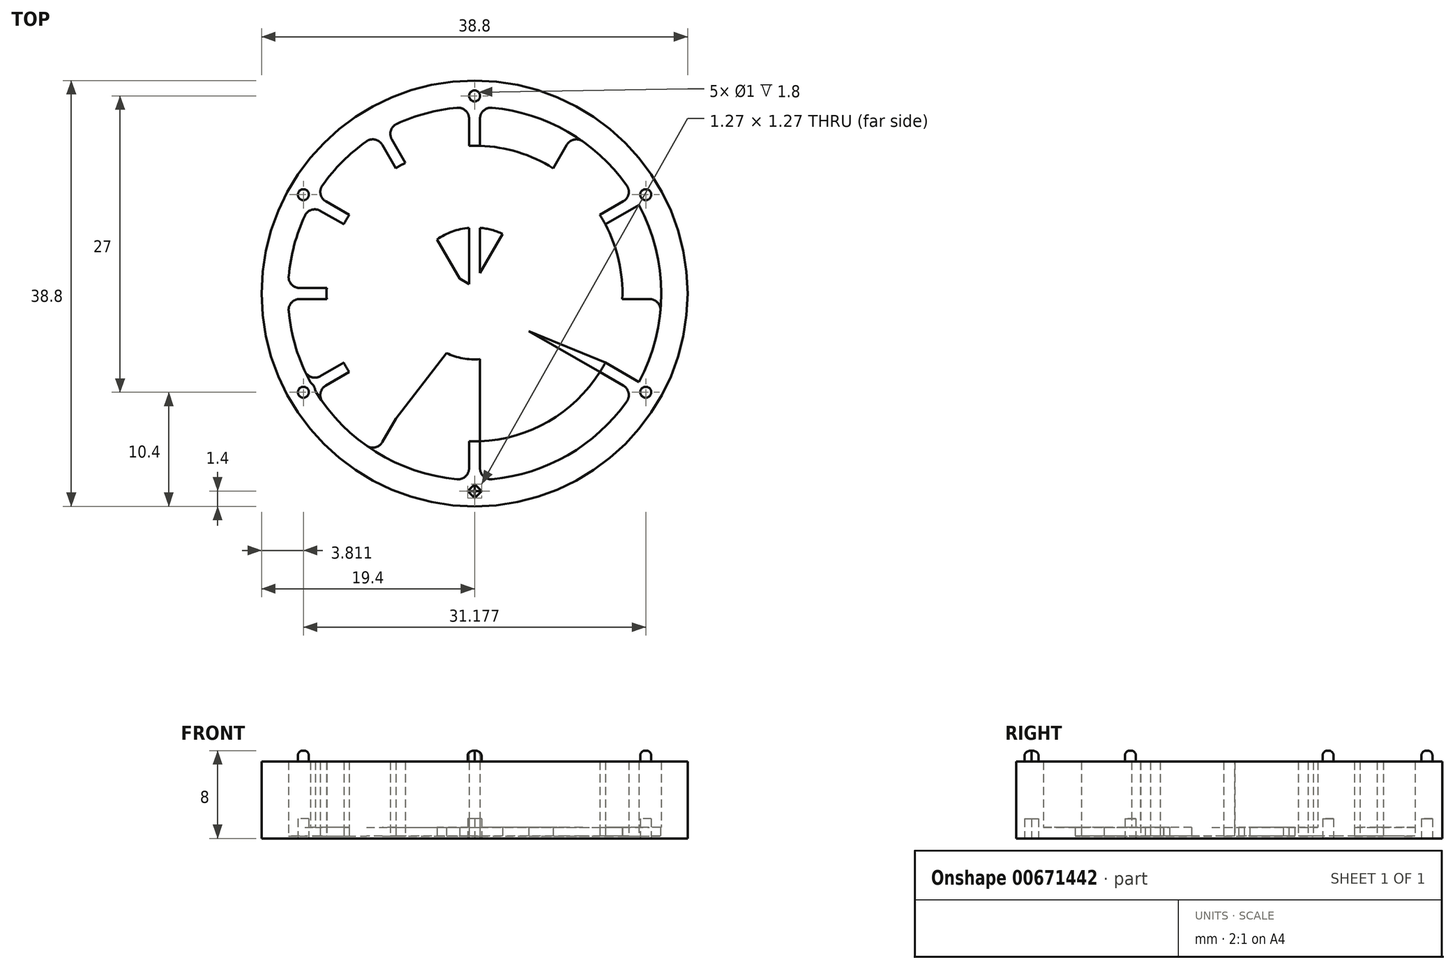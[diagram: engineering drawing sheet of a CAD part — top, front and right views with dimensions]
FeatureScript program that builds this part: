
annotation { "Feature Type Name" : "Feature", "Feature Type Description" : "" }
export const myFeature = defineFeature(function(context is Context, id is Id, definition is map)
    precondition{}
    {
        {
            var Q0;
            Q0=qCreatedBy(makeId("Top.planeOp"),FACE);
            var sketch = newSketch(context, id + "F0", { "sketchPlane" : qUnion([Q0])});
            skCircle(sketch, "E0", {"center": v(0, 0) * mm, "radius": 18 * mm});
            skCircle(sketch, "E1.0", {"center": v(0, 0) * mm, "radius": 17 * mm});
            skLineSegment(sketch, "E2.bottom", {"start": v(8.56, 15.83) * mm, "end": v(9.43, 15.33) * mm});
            skLineSegment(sketch, "E2.top", {"start": v(-9.43, -15.33) * mm, "end": v(-8.56, -15.83) * mm});
            skLineSegment(sketch, "E2.left", {"start": v(8.56, 15.83) * mm, "end": v(-9.43, -15.33) * mm});
            skLineSegment(sketch, "E2.right", {"start": v(9.43, 15.33) * mm, "end": v(-8.56, -15.83) * mm});
            skLineSegment(sketch, "E3.bottom", {"start": v(15.33, 9.43) * mm, "end": v(15.83, 8.56) * mm});
            skLineSegment(sketch, "E3.top", {"start": v(-15.83, -8.56) * mm, "end": v(-15.33, -9.43) * mm});
            skLineSegment(sketch, "E3.left", {"start": v(15.33, 9.43) * mm, "end": v(-15.83, -8.56) * mm});
            skLineSegment(sketch, "E3.right", {"start": v(15.83, 8.56) * mm, "end": v(-15.33, -9.43) * mm});
            skLineSegment(sketch, "E4", {"start": v(-38.35, 0) * mm, "end": v(39.17, 0) * mm, "construction": true});
            skLineSegment(sketch, "E5", {"start": v(0, 42.5) * mm, "end": v(0, -42.47) * mm, "construction": true});
            skLineSegment(sketch, "E6.bottom", {"start": v(-18, 0.5) * mm, "end": v(18, 0.5) * mm});
            skLineSegment(sketch, "E6.top", {"start": v(-18, -0.5) * mm, "end": v(18, -0.5) * mm});
            skLineSegment(sketch, "E6.left", {"start": v(-18, 0.5) * mm, "end": v(-18, -0.5) * mm});
            skLineSegment(sketch, "E6.right", {"start": v(18, 0.5) * mm, "end": v(18, -0.5) * mm});
            skLineSegment(sketch, "E7.bottom", {"start": v(-15.33, 9.43) * mm, "end": v(15.83, -8.56) * mm});
            skLineSegment(sketch, "E7.top", {"start": v(-15.83, 8.56) * mm, "end": v(15.33, -9.43) * mm});
            skLineSegment(sketch, "E7.left", {"start": v(-15.33, 9.43) * mm, "end": v(-15.83, 8.56) * mm});
            skLineSegment(sketch, "E7.right", {"start": v(15.83, -8.56) * mm, "end": v(15.33, -9.43) * mm});
            skLineSegment(sketch, "E8.bottom", {"start": v(-0.5, 18) * mm, "end": v(0.5, 18) * mm});
            skLineSegment(sketch, "E8.top", {"start": v(-0.5, -18) * mm, "end": v(0.5, -18) * mm});
            skLineSegment(sketch, "E8.left", {"start": v(-0.5, 18) * mm, "end": v(-0.5, -18) * mm});
            skLineSegment(sketch, "E8.right", {"start": v(0.5, 18) * mm, "end": v(0.5, -18) * mm});
            skLineSegment(sketch, "E9.bottom", {"start": v(-9.43, 15.33) * mm, "end": v(-8.56, 15.83) * mm});
            skLineSegment(sketch, "E9.top", {"start": v(8.56, -15.83) * mm, "end": v(9.43, -15.33) * mm});
            skLineSegment(sketch, "E9.left", {"start": v(-9.43, 15.33) * mm, "end": v(8.56, -15.83) * mm});
            skLineSegment(sketch, "E9.right", {"start": v(-8.56, 15.83) * mm, "end": v(9.43, -15.33) * mm});
            skCircle(sketch, "E10", {"center": v(0, 0) * mm, "radius": 13.47 * mm});
            skCircle(sketch, "E11", {"center": v(0, 0) * mm, "radius": 6 * mm});
            skLineSegment(sketch, "E12", {"start": v(-7.16, -11.4) * mm, "end": v(-2.56, -5.43) * mm});
            skLineSegment(sketch, "E13", {"start": v(4.93, -3.42) * mm, "end": v(11.9, -6.3) * mm});
            skSolve(sketch);
        }
        {
            var Q0;
            Q0=qCreatedBy(makeId("Top.planeOp"),FACE);
            var sketch = newSketch(context, id + "F1", { "sketchPlane" : qUnion([Q0])});
            skCircle(sketch, "E14", {"center": v(0, 0) * mm, "radius": 19.4 * mm});
            skCircle(sketch, "E15", {"center": v(0, 0) * mm, "radius": 17 * mm});
            skSolve(sketch);
        }
        {
            var Q0;
            Q0=makeQuery(id+"F1.imprint","IMPRINT",FACE,{"disambiguationData":[TD([[makeQuery(id+"F1.imprint","IMPRINT",EDGE,{"derivedFrom":sQuery(id+"F1.wireOp",EDGE,"E14")}),1.0]])]});
            extrude(context, id + "F2", {"entities" : qUnion([Q0]), "depth" : 7 * mm, "offsetDistance" : 25 * mm});
        }
        {
            var Q0;
            {var subQ0=sQuery(id+"F0.wireOp",EDGE,"E7.bottom");var subQ1=sQuery(id+"F0.wireOp",EDGE,"E1.0");var subQ2=makeQuery(id+"F0.imprint","INTERSECT",VERTEX,{"disambiguationData":[OD(0.0)],"derivedFrom":[subQ1,subQ0]});Q0=makeQuery(id+"F0.imprint","IMPRINT",FACE,{"disambiguationData":[TD([[makeQuery(id+"F0.imprint","IMPRINT",EDGE,{"disambiguationData":[TD([[subQ2,-1.0]])],"derivedFrom":subQ1}),1.0]])]});}
            var Q1;
            {var subQ0=sQuery(id+"F0.wireOp",EDGE,"E8.left");var subQ1=sQuery(id+"F0.wireOp",EDGE,"E1.0");var subQ2=makeQuery(id+"F0.imprint","INTERSECT",VERTEX,{"disambiguationData":[OD(1.0)],"derivedFrom":[subQ1,subQ0]});Q1=makeQuery(id+"F0.imprint","IMPRINT",FACE,{"disambiguationData":[TD([[makeQuery(id+"F0.imprint","IMPRINT",EDGE,{"disambiguationData":[TD([[subQ2,-1.0]])],"derivedFrom":subQ1}),1.0]])]});}
            var Q2;
            {var subQ0=sQuery(id+"F0.wireOp",EDGE,"E9.right");var subQ1=sQuery(id+"F0.wireOp",EDGE,"E1.0");var subQ2=makeQuery(id+"F0.imprint","INTERSECT",VERTEX,{"disambiguationData":[OD(0.0)],"derivedFrom":[subQ1,subQ0]});Q2=makeQuery(id+"F0.imprint","IMPRINT",FACE,{"disambiguationData":[TD([[makeQuery(id+"F0.imprint","IMPRINT",EDGE,{"disambiguationData":[TD([[subQ2,-1.0]])],"derivedFrom":subQ1}),1.0]])]});}
            var Q3;
            {var subQ0=sQuery(id+"F0.wireOp",EDGE,"E8.right");var subQ1=sQuery(id+"F0.wireOp",EDGE,"E1.0");var subQ2=makeQuery(id+"F0.imprint","INTERSECT",VERTEX,{"disambiguationData":[OD(0.0)],"derivedFrom":[subQ1,subQ0]});Q3=makeQuery(id+"F0.imprint","IMPRINT",FACE,{"disambiguationData":[TD([[makeQuery(id+"F0.imprint","IMPRINT",EDGE,{"disambiguationData":[TD([[subQ2,-1.0]])],"derivedFrom":subQ1}),1.0]])]});}
            var Q4;
            {var subQ0=sQuery(id+"F0.wireOp",EDGE,"E3.right");var subQ1=sQuery(id+"F0.wireOp",EDGE,"E1.0");var subQ2=makeQuery(id+"F0.imprint","INTERSECT",VERTEX,{"disambiguationData":[OD(0.0)],"derivedFrom":[subQ1,subQ0]});Q4=makeQuery(id+"F0.imprint","IMPRINT",FACE,{"disambiguationData":[TD([[makeQuery(id+"F0.imprint","IMPRINT",EDGE,{"disambiguationData":[TD([[subQ2,-1.0]])],"derivedFrom":subQ1}),1.0]])]});}
            var Q5;
            {var subQ0=sQuery(id+"F0.wireOp",EDGE,"E7.top");var subQ1=sQuery(id+"F0.wireOp",EDGE,"E1.0");var subQ2=makeQuery(id+"F0.imprint","INTERSECT",VERTEX,{"disambiguationData":[OD(1.0)],"derivedFrom":[subQ1,subQ0]});Q5=makeQuery(id+"F0.imprint","IMPRINT",FACE,{"disambiguationData":[TD([[makeQuery(id+"F0.imprint","IMPRINT",EDGE,{"disambiguationData":[TD([[subQ2,-1.0]])],"derivedFrom":subQ1}),1.0]])]});}
            var Q6;
            {var subQ0=sQuery(id+"F0.wireOp",EDGE,"E6.bottom");var subQ1=sQuery(id+"F0.wireOp",EDGE,"E1.0");var subQ2=makeQuery(id+"F0.imprint","INTERSECT",VERTEX,{"disambiguationData":[OD(1.0)],"derivedFrom":[subQ1,subQ0]});Q6=makeQuery(id+"F0.imprint","IMPRINT",FACE,{"disambiguationData":[TD([[makeQuery(id+"F0.imprint","IMPRINT",EDGE,{"disambiguationData":[TD([[subQ2,-1.0]])],"derivedFrom":subQ1}),1.0]])]});}
            extrude(context, id + "F3", {"entities" : qUnion([Q0, Q1, Q2, Q3, Q4, Q5, Q6]), "operationType" : NewBodyOperationType.ADD, "depth" : 7 * mm, "offsetDistance" : 25 * mm});
        }
        {
            var Q0;
            Q0=makeQuery(id+"F1.imprint","IMPRINT",FACE,{"disambiguationData":[TD([[makeQuery(id+"F1.imprint","IMPRINT",EDGE,{"derivedFrom":sQuery(id+"F1.wireOp",EDGE,"E14")}),1.0]])]});
            var Q1;
            Q1=makeQuery(id+"F1.imprint","IMPRINT",FACE,{"disambiguationData":[TD([[makeQuery(id+"F1.imprint","IMPRINT",EDGE,{"derivedFrom":sQuery(id+"F1.wireOp",EDGE,"E15")}),1.0]])]});
            extrude(context, id + "F4", {"entities" : qUnion([Q0, Q1]), "operationType" : NewBodyOperationType.ADD, "depth" : 1 * mm, "offsetDistance" : 25 * mm});
        }
        {
            var Q0;
            Q0=qCreatedBy(makeId("Top.planeOp"),FACE);
            var sketch = newSketch(context, id + "F5", { "sketchPlane" : qUnion([Q0])});
            skCircle(sketch, "E16", {"center": v(0, 0) * mm, "radius": 18 * mm});
            skLineSegment(sketch, "E17", {"start": v(0, 18) * mm, "end": v(0, -18) * mm, "construction": true});
            skLineSegment(sketch, "E18", {"start": v(15.59, 9) * mm, "end": v(0, 0) * mm, "construction": true});
            skLineSegment(sketch, "E19", {"start": v(9, 15.59) * mm, "end": v(0, 0) * mm, "construction": true});
            skLineSegment(sketch, "E20", {"start": v(0, 0) * mm, "end": v(18, 0) * mm, "construction": true});
            skLineSegment(sketch, "E21", {"start": v(0, 0) * mm, "end": v(15.59, -9) * mm, "construction": true});
            skLineSegment(sketch, "E22", {"start": v(0, 0) * mm, "end": v(9, -15.59) * mm, "construction": true});
            skLineSegment(sketch, "E23", {"start": v(0, 0) * mm, "end": v(-9, 15.59) * mm, "construction": true});
            skLineSegment(sketch, "E24", {"start": v(0, 0) * mm, "end": v(-15.59, 9) * mm, "construction": true});
            skLineSegment(sketch, "E25", {"start": v(0, 0) * mm, "end": v(-18, 0) * mm, "construction": true});
            skLineSegment(sketch, "E26", {"start": v(0, 0) * mm, "end": v(-15.59, -9) * mm, "construction": true});
            skLineSegment(sketch, "E27", {"start": v(0, 0) * mm, "end": v(-9, -15.59) * mm, "construction": true});
            skCircle(sketch, "E28", {"center": v(0, 18) * mm, "radius": 1.1 * mm});
            skCircle(sketch, "E29", {"center": v(15.59, 9) * mm, "radius": 1.1 * mm});
            skCircle(sketch, "E30", {"center": v(15.59, -9) * mm, "radius": 1.1 * mm});
            skCircle(sketch, "E31", {"center": v(0, -18) * mm, "radius": 1.1 * mm});
            skCircle(sketch, "E32", {"center": v(-15.59, -9) * mm, "radius": 1.1 * mm});
            skCircle(sketch, "E33", {"center": v(-15.59, 9) * mm, "radius": 1.1 * mm});
            skCircle(sketch, "E34", {"center": v(-15.59, 9) * mm, "radius": 0.5 * mm});
            skCircle(sketch, "E35", {"center": v(0, 18) * mm, "radius": 0.5 * mm});
            skCircle(sketch, "E36", {"center": v(15.59, 9) * mm, "radius": 0.5 * mm});
            skCircle(sketch, "E37", {"center": v(15.59, -9) * mm, "radius": 0.5 * mm});
            skCircle(sketch, "E38", {"center": v(-15.59, -9) * mm, "radius": 0.5 * mm});
            skLineSegment(sketch, "E39.bottom", {"start": v(0.64, -18) * mm, "end": v(0, -18.64) * mm});
            skLineSegment(sketch, "E39.top", {"start": v(0, -17.36) * mm, "end": v(-0.64, -18) * mm});
            skLineSegment(sketch, "E39.left", {"start": v(0.64, -18) * mm, "end": v(0, -17.36) * mm});
            skLineSegment(sketch, "E39.right", {"start": v(0, -18.64) * mm, "end": v(-0.64, -18) * mm});
            skSolve(sketch);
        }
        {
            var Q0;
            {var subQ0=sQuery(id+"F5.wireOp",EDGE,"E33");var subQ1=sQuery(id+"F5.wireOp",EDGE,"E16");var subQ2=makeQuery(id+"F5.imprint","INTERSECT",VERTEX,{"disambiguationData":[OD(0.0)],"derivedFrom":[subQ1,subQ0]});Q0=makeQuery(id+"F5.imprint","IMPRINT",FACE,{"disambiguationData":[TD([[makeQuery(id+"F5.imprint","IMPRINT",EDGE,{"disambiguationData":[TD([[subQ2,-1.0]])],"derivedFrom":subQ1}),1.0]])]});}
            var Q1;
            {var subQ0=sQuery(id+"F5.wireOp",EDGE,"E33");var subQ1=sQuery(id+"F5.wireOp",EDGE,"E16");var subQ2=makeQuery(id+"F5.imprint","INTERSECT",VERTEX,{"disambiguationData":[OD(0.0)],"derivedFrom":[subQ1,subQ0]});Q1=makeQuery(id+"F5.imprint","IMPRINT",FACE,{"disambiguationData":[TD([[makeQuery(id+"F5.imprint","IMPRINT",EDGE,{"disambiguationData":[TD([[subQ2,-1.0]])],"derivedFrom":subQ1}),-1.0]])]});}
            var Q2;
            {var subQ0=sQuery(id+"F5.wireOp",EDGE,"E28");var subQ1=sQuery(id+"F5.wireOp",EDGE,"E16");var subQ2=makeQuery(id+"F5.imprint","INTERSECT",VERTEX,{"disambiguationData":[OD(0.0)],"derivedFrom":[subQ1,subQ0]});Q2=makeQuery(id+"F5.imprint","IMPRINT",FACE,{"disambiguationData":[TD([[makeQuery(id+"F5.imprint","IMPRINT",EDGE,{"disambiguationData":[TD([[subQ2,-1.0]])],"derivedFrom":subQ1}),1.0]])]});}
            var Q3;
            {var subQ0=sQuery(id+"F5.wireOp",EDGE,"E28");var subQ1=sQuery(id+"F5.wireOp",EDGE,"E16");var subQ2=makeQuery(id+"F5.imprint","INTERSECT",VERTEX,{"disambiguationData":[OD(0.0)],"derivedFrom":[subQ1,subQ0]});Q3=makeQuery(id+"F5.imprint","IMPRINT",FACE,{"disambiguationData":[TD([[makeQuery(id+"F5.imprint","IMPRINT",EDGE,{"disambiguationData":[TD([[subQ2,-1.0]])],"derivedFrom":subQ1}),-1.0]])]});}
            var Q4;
            {var subQ0=sQuery(id+"F5.wireOp",EDGE,"E29");var subQ1=sQuery(id+"F5.wireOp",EDGE,"E16");var subQ2=makeQuery(id+"F5.imprint","INTERSECT",VERTEX,{"disambiguationData":[OD(0.0)],"derivedFrom":[subQ1,subQ0]});Q4=makeQuery(id+"F5.imprint","IMPRINT",FACE,{"disambiguationData":[TD([[makeQuery(id+"F5.imprint","IMPRINT",EDGE,{"disambiguationData":[TD([[subQ2,-1.0]])],"derivedFrom":subQ1}),-1.0]])]});}
            var Q5;
            {var subQ0=sQuery(id+"F5.wireOp",EDGE,"E29");var subQ1=sQuery(id+"F5.wireOp",EDGE,"E16");var subQ2=makeQuery(id+"F5.imprint","INTERSECT",VERTEX,{"disambiguationData":[OD(0.0)],"derivedFrom":[subQ1,subQ0]});Q5=makeQuery(id+"F5.imprint","IMPRINT",FACE,{"disambiguationData":[TD([[makeQuery(id+"F5.imprint","IMPRINT",EDGE,{"disambiguationData":[TD([[subQ2,-1.0]])],"derivedFrom":subQ1}),1.0]])]});}
            var Q6;
            {var subQ0=sQuery(id+"F5.wireOp",EDGE,"E32");var subQ1=sQuery(id+"F5.wireOp",EDGE,"E16");var subQ2=makeQuery(id+"F5.imprint","INTERSECT",VERTEX,{"disambiguationData":[OD(0.0)],"derivedFrom":[subQ1,subQ0]});Q6=makeQuery(id+"F5.imprint","IMPRINT",FACE,{"disambiguationData":[TD([[makeQuery(id+"F5.imprint","IMPRINT",EDGE,{"disambiguationData":[TD([[subQ2,-1.0]])],"derivedFrom":subQ1}),1.0]])]});}
            var Q7;
            {var subQ0=sQuery(id+"F5.wireOp",EDGE,"E32");var subQ1=sQuery(id+"F5.wireOp",EDGE,"E16");var subQ2=makeQuery(id+"F5.imprint","INTERSECT",VERTEX,{"disambiguationData":[OD(0.0)],"derivedFrom":[subQ1,subQ0]});Q7=makeQuery(id+"F5.imprint","IMPRINT",FACE,{"disambiguationData":[TD([[makeQuery(id+"F5.imprint","IMPRINT",EDGE,{"disambiguationData":[TD([[subQ2,-1.0]])],"derivedFrom":subQ1}),-1.0]])]});}
            var Q8;
            {var subQ3=sQuery(id+"F5.wireOp",EDGE,"E16");var subQ5=sQuery(id+"F5.wireOp",EDGE,"E31");var subQ6=makeQuery(id+"F5.imprint","INTERSECT",VERTEX,{"disambiguationData":[OD(0.0)],"derivedFrom":[subQ3,subQ5]});Q8=makeQuery(id+"F5.imprint","IMPRINT",FACE,{"disambiguationData":[TD([[makeQuery(id+"F5.imprint","IMPRINT",EDGE,{"disambiguationData":[TD([[subQ6,-1.0]])],"derivedFrom":subQ3}),1.0]])]});}
            var Q9;
            {var subQ6=sQuery(id+"F5.wireOp",EDGE,"E39.bottom");Q9=makeQuery(id+"F5.imprint","IMPRINT",FACE,{"disambiguationData":[TD([[makeQuery(id+"F5.imprint","IMPRINT",EDGE,{"derivedFrom":subQ6}),1.0]])]});}
            var Q10;
            {var subQ0=sQuery(id+"F5.wireOp",EDGE,"E30");var subQ1=sQuery(id+"F5.wireOp",EDGE,"E16");var subQ2=makeQuery(id+"F5.imprint","INTERSECT",VERTEX,{"disambiguationData":[OD(0.0)],"derivedFrom":[subQ1,subQ0]});Q10=makeQuery(id+"F5.imprint","IMPRINT",FACE,{"disambiguationData":[TD([[makeQuery(id+"F5.imprint","IMPRINT",EDGE,{"disambiguationData":[TD([[subQ2,-1.0]])],"derivedFrom":subQ1}),-1.0]])]});}
            var Q11;
            {var subQ0=sQuery(id+"F5.wireOp",EDGE,"E30");var subQ1=sQuery(id+"F5.wireOp",EDGE,"E16");var subQ2=makeQuery(id+"F5.imprint","INTERSECT",VERTEX,{"disambiguationData":[OD(0.0)],"derivedFrom":[subQ1,subQ0]});Q11=makeQuery(id+"F5.imprint","IMPRINT",FACE,{"disambiguationData":[TD([[makeQuery(id+"F5.imprint","IMPRINT",EDGE,{"disambiguationData":[TD([[subQ2,-1.0]])],"derivedFrom":subQ1}),1.0]])]});}
            var Q12;
            {var subQ0=sQuery(id+"F5.wireOp",EDGE,"E34");var subQ1=sQuery(id+"F5.wireOp",EDGE,"E16");var subQ2=makeQuery(id+"F5.imprint","INTERSECT",VERTEX,{"disambiguationData":[OD(0.0)],"derivedFrom":[subQ1,subQ0]});Q12=makeQuery(id+"F5.imprint","IMPRINT",FACE,{"disambiguationData":[TD([[makeQuery(id+"F5.imprint","IMPRINT",EDGE,{"disambiguationData":[TD([[subQ2,-1.0]])],"derivedFrom":subQ1}),1.0]])]});}
            var Q13;
            {var subQ0=sQuery(id+"F5.wireOp",EDGE,"E34");var subQ1=sQuery(id+"F5.wireOp",EDGE,"E16");var subQ2=makeQuery(id+"F5.imprint","INTERSECT",VERTEX,{"disambiguationData":[OD(0.0)],"derivedFrom":[subQ1,subQ0]});Q13=makeQuery(id+"F5.imprint","IMPRINT",FACE,{"disambiguationData":[TD([[makeQuery(id+"F5.imprint","IMPRINT",EDGE,{"disambiguationData":[TD([[subQ2,-1.0]])],"derivedFrom":subQ1}),-1.0]])]});}
            var Q14;
            {var subQ0=sQuery(id+"F5.wireOp",EDGE,"E35");var subQ1=sQuery(id+"F5.wireOp",EDGE,"E16");var subQ2=makeQuery(id+"F5.imprint","INTERSECT",VERTEX,{"disambiguationData":[OD(0.0)],"derivedFrom":[subQ1,subQ0]});Q14=makeQuery(id+"F5.imprint","IMPRINT",FACE,{"disambiguationData":[TD([[makeQuery(id+"F5.imprint","IMPRINT",EDGE,{"disambiguationData":[TD([[subQ2,-1.0]])],"derivedFrom":subQ1}),-1.0]])]});}
            var Q15;
            {var subQ0=sQuery(id+"F5.wireOp",EDGE,"E35");var subQ1=sQuery(id+"F5.wireOp",EDGE,"E16");var subQ2=makeQuery(id+"F5.imprint","INTERSECT",VERTEX,{"disambiguationData":[OD(0.0)],"derivedFrom":[subQ1,subQ0]});Q15=makeQuery(id+"F5.imprint","IMPRINT",FACE,{"disambiguationData":[TD([[makeQuery(id+"F5.imprint","IMPRINT",EDGE,{"disambiguationData":[TD([[subQ2,-1.0]])],"derivedFrom":subQ1}),1.0]])]});}
            var Q16;
            {var subQ0=sQuery(id+"F5.wireOp",EDGE,"E36");var subQ1=sQuery(id+"F5.wireOp",EDGE,"E16");var subQ2=makeQuery(id+"F5.imprint","INTERSECT",VERTEX,{"disambiguationData":[OD(0.0)],"derivedFrom":[subQ1,subQ0]});Q16=makeQuery(id+"F5.imprint","IMPRINT",FACE,{"disambiguationData":[TD([[makeQuery(id+"F5.imprint","IMPRINT",EDGE,{"disambiguationData":[TD([[subQ2,-1.0]])],"derivedFrom":subQ1}),-1.0]])]});}
            var Q17;
            {var subQ0=sQuery(id+"F5.wireOp",EDGE,"E36");var subQ1=sQuery(id+"F5.wireOp",EDGE,"E16");var subQ2=makeQuery(id+"F5.imprint","INTERSECT",VERTEX,{"disambiguationData":[OD(0.0)],"derivedFrom":[subQ1,subQ0]});Q17=makeQuery(id+"F5.imprint","IMPRINT",FACE,{"disambiguationData":[TD([[makeQuery(id+"F5.imprint","IMPRINT",EDGE,{"disambiguationData":[TD([[subQ2,-1.0]])],"derivedFrom":subQ1}),1.0]])]});}
            var Q18;
            {var subQ0=sQuery(id+"F5.wireOp",EDGE,"E37");var subQ1=sQuery(id+"F5.wireOp",EDGE,"E16");var subQ2=makeQuery(id+"F5.imprint","INTERSECT",VERTEX,{"disambiguationData":[OD(0.0)],"derivedFrom":[subQ1,subQ0]});Q18=makeQuery(id+"F5.imprint","IMPRINT",FACE,{"disambiguationData":[TD([[makeQuery(id+"F5.imprint","IMPRINT",EDGE,{"disambiguationData":[TD([[subQ2,-1.0]])],"derivedFrom":subQ1}),-1.0]])]});}
            var Q19;
            {var subQ0=sQuery(id+"F5.wireOp",EDGE,"E37");var subQ1=sQuery(id+"F5.wireOp",EDGE,"E16");var subQ2=makeQuery(id+"F5.imprint","INTERSECT",VERTEX,{"disambiguationData":[OD(0.0)],"derivedFrom":[subQ1,subQ0]});Q19=makeQuery(id+"F5.imprint","IMPRINT",FACE,{"disambiguationData":[TD([[makeQuery(id+"F5.imprint","IMPRINT",EDGE,{"disambiguationData":[TD([[subQ2,-1.0]])],"derivedFrom":subQ1}),1.0]])]});}
            var Q20;
            {var subQ1=sQuery(id+"F5.wireOp",EDGE,"E39.bottom");Q20=makeQuery(id+"F5.imprint","IMPRINT",FACE,{"disambiguationData":[TD([[makeQuery(id+"F5.imprint","IMPRINT",EDGE,{"derivedFrom":subQ1}),-1.0]])]});}
            var Q21;
            {var subQ0=sQuery(id+"F5.wireOp",EDGE,"E38");var subQ1=sQuery(id+"F5.wireOp",EDGE,"E16");var subQ2=makeQuery(id+"F5.imprint","INTERSECT",VERTEX,{"disambiguationData":[OD(0.0)],"derivedFrom":[subQ1,subQ0]});Q21=makeQuery(id+"F5.imprint","IMPRINT",FACE,{"disambiguationData":[TD([[makeQuery(id+"F5.imprint","IMPRINT",EDGE,{"disambiguationData":[TD([[subQ2,-1.0]])],"derivedFrom":subQ1}),-1.0]])]});}
            var Q22;
            {var subQ0=sQuery(id+"F5.wireOp",EDGE,"E38");var subQ1=sQuery(id+"F5.wireOp",EDGE,"E16");var subQ2=makeQuery(id+"F5.imprint","INTERSECT",VERTEX,{"disambiguationData":[OD(0.0)],"derivedFrom":[subQ1,subQ0]});Q22=makeQuery(id+"F5.imprint","IMPRINT",FACE,{"disambiguationData":[TD([[makeQuery(id+"F5.imprint","IMPRINT",EDGE,{"disambiguationData":[TD([[subQ2,-1.0]])],"derivedFrom":subQ1}),1.0]])]});}
            var Q23;
            {var subQ0=sQuery(id+"F5.wireOp",EDGE,"E39.top");var subQ1=sQuery(id+"F5.wireOp",EDGE,"E16");var subQ2=makeQuery(id+"F5.imprint","INTERSECT",VERTEX,{"derivedFrom":[subQ1,subQ0]});Q23=makeQuery(id+"F5.imprint","IMPRINT",FACE,{"disambiguationData":[TD([[makeQuery(id+"F5.imprint","IMPRINT",EDGE,{"disambiguationData":[TD([[subQ2,-1.0]])],"derivedFrom":subQ1}),1.0]])]});}
            extrude(context, id + "F6", {"entities" : qUnion([Q0, Q1, Q2, Q3, Q4, Q5, Q6, Q7, Q8, Q9, Q10, Q11, Q12, Q13, Q14, Q15, Q16, Q17, Q18, Q19, Q20, Q21, Q22, Q23]), "operationType" : NewBodyOperationType.ADD, "depth" : 7 * mm, "offsetDistance" : 25 * mm});
        }
        {
            var Q0;
            {var subQ0=sQuery(id+"F0.wireOp",EDGE,"E8.right");var subQ1=sQuery(id+"F0.wireOp",EDGE,"E1.0");Q0=makeQuery(id+"F3.opExtrude","SWEPT_EDGE",EDGE,{"disambiguationData":[OSD([subQ1,subQ0]),TDD([makeQuery(id+"F0.imprint","INTERSECT",VERTEX,{"disambiguationData":[OD(1.0)],"derivedFrom":[subQ1,subQ0]})])]});}
            var Q1;
            {var subQ0=sQuery(id+"F0.wireOp",EDGE,"E2.left");var subQ1=sQuery(id+"F0.wireOp",EDGE,"E1.0");Q1=makeQuery(id+"F3.opExtrude","SWEPT_EDGE",EDGE,{"disambiguationData":[OSD([subQ1,subQ0]),TDD([makeQuery(id+"F0.imprint","INTERSECT",VERTEX,{"disambiguationData":[OD(1.0)],"derivedFrom":[subQ1,subQ0]})])]});}
            var Q2;
            {var subQ0=sQuery(id+"F0.wireOp",EDGE,"E3.left");var subQ1=sQuery(id+"F0.wireOp",EDGE,"E1.0");Q2=makeQuery(id+"F3.opExtrude","SWEPT_EDGE",EDGE,{"disambiguationData":[OSD([subQ1,subQ0]),TDD([makeQuery(id+"F0.imprint","INTERSECT",VERTEX,{"disambiguationData":[OD(1.0)],"derivedFrom":[subQ1,subQ0]})])]});}
            var Q3;
            {var subQ0=sQuery(id+"F0.wireOp",EDGE,"E6.bottom");var subQ1=sQuery(id+"F0.wireOp",EDGE,"E1.0");Q3=makeQuery(id+"F3.opExtrude","SWEPT_EDGE",EDGE,{"disambiguationData":[OSD([subQ1,subQ0]),TDD([makeQuery(id+"F0.imprint","INTERSECT",VERTEX,{"disambiguationData":[OD(1.0)],"derivedFrom":[subQ1,subQ0]})])]});}
            var Q4;
            {var subQ0=sQuery(id+"F0.wireOp",EDGE,"E9.right");var subQ1=sQuery(id+"F0.wireOp",EDGE,"E1.0");Q4=makeQuery(id+"F3.opExtrude","SWEPT_EDGE",EDGE,{"disambiguationData":[OSD([subQ1,subQ0]),TDD([makeQuery(id+"F0.imprint","INTERSECT",VERTEX,{"disambiguationData":[OD(1.0)],"derivedFrom":[subQ1,subQ0]})])]});}
            var Q5;
            {var subQ0=sQuery(id+"F0.wireOp",EDGE,"E7.bottom");var subQ1=sQuery(id+"F0.wireOp",EDGE,"E1.0");Q5=makeQuery(id+"F3.opExtrude","SWEPT_EDGE",EDGE,{"disambiguationData":[OSD([subQ1,subQ0]),TDD([makeQuery(id+"F0.imprint","INTERSECT",VERTEX,{"disambiguationData":[OD(1.0)],"derivedFrom":[subQ1,subQ0]})])]});}
            var Q6;
            {var subQ0=sQuery(id+"F0.wireOp",EDGE,"E8.left");var subQ1=sQuery(id+"F0.wireOp",EDGE,"E1.0");Q6=makeQuery(id+"F3.opExtrude","SWEPT_EDGE",EDGE,{"disambiguationData":[OSD([subQ1,subQ0]),TDD([makeQuery(id+"F0.imprint","INTERSECT",VERTEX,{"disambiguationData":[OD(0.0)],"derivedFrom":[subQ1,subQ0]})])]});}
            var Q7;
            {var subQ0=sQuery(id+"F0.wireOp",EDGE,"E2.left");var subQ1=sQuery(id+"F0.wireOp",EDGE,"E1.0");Q7=makeQuery(id+"F3.opExtrude","SWEPT_EDGE",EDGE,{"disambiguationData":[OSD([subQ1,subQ0]),TDD([makeQuery(id+"F0.imprint","INTERSECT",VERTEX,{"disambiguationData":[OD(0.0)],"derivedFrom":[subQ1,subQ0]})])]});}
            var Q8;
            {var subQ0=sQuery(id+"F0.wireOp",EDGE,"E3.left");var subQ1=sQuery(id+"F0.wireOp",EDGE,"E1.0");Q8=makeQuery(id+"F3.opExtrude","SWEPT_EDGE",EDGE,{"disambiguationData":[OSD([subQ1,subQ0]),TDD([makeQuery(id+"F0.imprint","INTERSECT",VERTEX,{"disambiguationData":[OD(0.0)],"derivedFrom":[subQ1,subQ0]})])]});}
            var Q9;
            {var subQ0=sQuery(id+"F0.wireOp",EDGE,"E6.top");var subQ1=sQuery(id+"F0.wireOp",EDGE,"E1.0");Q9=makeQuery(id+"F3.opExtrude","SWEPT_EDGE",EDGE,{"disambiguationData":[OSD([subQ1,subQ0]),TDD([makeQuery(id+"F0.imprint","INTERSECT",VERTEX,{"disambiguationData":[OD(1.0)],"derivedFrom":[subQ1,subQ0]})])]});}
            var Q10;
            {var subQ0=sQuery(id+"F0.wireOp",EDGE,"E7.top");var subQ1=sQuery(id+"F0.wireOp",EDGE,"E1.0");Q10=makeQuery(id+"F3.opExtrude","SWEPT_EDGE",EDGE,{"disambiguationData":[OSD([subQ1,subQ0]),TDD([makeQuery(id+"F0.imprint","INTERSECT",VERTEX,{"disambiguationData":[OD(0.0)],"derivedFrom":[subQ1,subQ0]})])]});}
            var Q11;
            {var subQ0=sQuery(id+"F0.wireOp",EDGE,"E6.top");var subQ1=sQuery(id+"F0.wireOp",EDGE,"E1.0");Q11=makeQuery(id+"F3.opExtrude","SWEPT_EDGE",EDGE,{"disambiguationData":[OSD([subQ1,subQ0]),TDD([makeQuery(id+"F0.imprint","INTERSECT",VERTEX,{"disambiguationData":[OD(0.0)],"derivedFrom":[subQ1,subQ0]})])]});}
            var Q12;
            {var subQ0=sQuery(id+"F0.wireOp",EDGE,"E9.left");var subQ1=sQuery(id+"F0.wireOp",EDGE,"E1.0");Q12=makeQuery(id+"F3.opExtrude","SWEPT_EDGE",EDGE,{"disambiguationData":[OSD([subQ1,subQ0]),TDD([makeQuery(id+"F0.imprint","INTERSECT",VERTEX,{"disambiguationData":[OD(0.0)],"derivedFrom":[subQ1,subQ0]})])]});}
            var Q13;
            {var subQ0=sQuery(id+"F0.wireOp",EDGE,"E8.right");var subQ1=sQuery(id+"F0.wireOp",EDGE,"E1.0");Q13=makeQuery(id+"F3.opExtrude","SWEPT_EDGE",EDGE,{"disambiguationData":[OSD([subQ1,subQ0]),TDD([makeQuery(id+"F0.imprint","INTERSECT",VERTEX,{"disambiguationData":[OD(0.0)],"derivedFrom":[subQ1,subQ0]})])]});}
            var Q14;
            {var subQ0=sQuery(id+"F0.wireOp",EDGE,"E7.bottom");var subQ1=sQuery(id+"F0.wireOp",EDGE,"E1.0");Q14=makeQuery(id+"F3.opExtrude","SWEPT_EDGE",EDGE,{"disambiguationData":[OSD([subQ1,subQ0]),TDD([makeQuery(id+"F0.imprint","INTERSECT",VERTEX,{"disambiguationData":[OD(0.0)],"derivedFrom":[subQ1,subQ0]})])]});}
            var Q15;
            {var subQ0=sQuery(id+"F0.wireOp",EDGE,"E9.right");var subQ1=sQuery(id+"F0.wireOp",EDGE,"E1.0");Q15=makeQuery(id+"F3.opExtrude","SWEPT_EDGE",EDGE,{"disambiguationData":[OSD([subQ1,subQ0]),TDD([makeQuery(id+"F0.imprint","INTERSECT",VERTEX,{"disambiguationData":[OD(0.0)],"derivedFrom":[subQ1,subQ0]})])]});}
            var Q16;
            {var subQ0=sQuery(id+"F0.wireOp",EDGE,"E3.right");var subQ1=sQuery(id+"F0.wireOp",EDGE,"E1.0");Q16=makeQuery(id+"F3.opExtrude","SWEPT_EDGE",EDGE,{"disambiguationData":[OSD([subQ1,subQ0]),TDD([makeQuery(id+"F0.imprint","INTERSECT",VERTEX,{"disambiguationData":[OD(1.0)],"derivedFrom":[subQ1,subQ0]})])]});}
            var Q17;
            {var subQ0=sQuery(id+"F0.wireOp",EDGE,"E2.right");var subQ1=sQuery(id+"F0.wireOp",EDGE,"E1.0");Q17=makeQuery(id+"F3.opExtrude","SWEPT_EDGE",EDGE,{"disambiguationData":[OSD([subQ1,subQ0]),TDD([makeQuery(id+"F0.imprint","INTERSECT",VERTEX,{"disambiguationData":[OD(1.0)],"derivedFrom":[subQ1,subQ0]})])]});}
            var Q18;
            {var subQ0=sQuery(id+"F0.wireOp",EDGE,"E3.right");var subQ1=sQuery(id+"F0.wireOp",EDGE,"E1.0");Q18=makeQuery(id+"F3.opExtrude","SWEPT_EDGE",EDGE,{"disambiguationData":[OSD([subQ1,subQ0]),TDD([makeQuery(id+"F0.imprint","INTERSECT",VERTEX,{"disambiguationData":[OD(0.0)],"derivedFrom":[subQ1,subQ0]})])]});}
            var Q19;
            {var subQ0=sQuery(id+"F0.wireOp",EDGE,"E2.right");var subQ1=sQuery(id+"F0.wireOp",EDGE,"E1.0");Q19=makeQuery(id+"F3.opExtrude","SWEPT_EDGE",EDGE,{"disambiguationData":[OSD([subQ1,subQ0]),TDD([makeQuery(id+"F0.imprint","INTERSECT",VERTEX,{"disambiguationData":[OD(0.0)],"derivedFrom":[subQ1,subQ0]})])]});}
            var Q20;
            {var subQ0=sQuery(id+"F0.wireOp",EDGE,"E8.left");var subQ1=sQuery(id+"F0.wireOp",EDGE,"E1.0");Q20=makeQuery(id+"F3.opExtrude","SWEPT_EDGE",EDGE,{"disambiguationData":[OSD([subQ1,subQ0]),TDD([makeQuery(id+"F0.imprint","INTERSECT",VERTEX,{"disambiguationData":[OD(1.0)],"derivedFrom":[subQ1,subQ0]})])]});}
            var Q21;
            {var subQ0=sQuery(id+"F0.wireOp",EDGE,"E9.left");var subQ1=sQuery(id+"F0.wireOp",EDGE,"E1.0");Q21=makeQuery(id+"F3.opExtrude","SWEPT_EDGE",EDGE,{"disambiguationData":[OSD([subQ1,subQ0]),TDD([makeQuery(id+"F0.imprint","INTERSECT",VERTEX,{"disambiguationData":[OD(1.0)],"derivedFrom":[subQ1,subQ0]})])]});}
            var Q22;
            {var subQ0=sQuery(id+"F0.wireOp",EDGE,"E7.top");var subQ1=sQuery(id+"F0.wireOp",EDGE,"E1.0");Q22=makeQuery(id+"F3.opExtrude","SWEPT_EDGE",EDGE,{"disambiguationData":[OSD([subQ1,subQ0]),TDD([makeQuery(id+"F0.imprint","INTERSECT",VERTEX,{"disambiguationData":[OD(1.0)],"derivedFrom":[subQ1,subQ0]})])]});}
            var Q23;
            {var subQ0=sQuery(id+"F0.wireOp",EDGE,"E6.bottom");var subQ1=sQuery(id+"F0.wireOp",EDGE,"E1.0");Q23=makeQuery(id+"F3.opExtrude","SWEPT_EDGE",EDGE,{"disambiguationData":[OSD([subQ1,subQ0]),TDD([makeQuery(id+"F0.imprint","INTERSECT",VERTEX,{"disambiguationData":[OD(0.0)],"derivedFrom":[subQ1,subQ0]})])]});}
            fillet(context, id + "F7", {"entities" : qUnion([Q0, Q1, Q2, Q3, Q4, Q5, Q6, Q7, Q8, Q9, Q10, Q11, Q12, Q13, Q14, Q15, Q16, Q17, Q18, Q19, Q20, Q21, Q22, Q23]), "radius" : 1 * mm, "tangentPropagation" : true, "allowEdgeOverflow" : false});
        }
        {
            var Q0;
            {var subQ0=sQuery(id+"F5.wireOp",EDGE,"E34");var subQ1=sQuery(id+"F5.wireOp",EDGE,"E16");var subQ2=makeQuery(id+"F5.imprint","INTERSECT",VERTEX,{"disambiguationData":[OD(0.0)],"derivedFrom":[subQ1,subQ0]});Q0=makeQuery(id+"F5.imprint","IMPRINT",FACE,{"disambiguationData":[TD([[makeQuery(id+"F5.imprint","IMPRINT",EDGE,{"disambiguationData":[TD([[subQ2,-1.0]])],"derivedFrom":subQ1}),-1.0]])]});}
            var Q1;
            {var subQ0=sQuery(id+"F5.wireOp",EDGE,"E34");var subQ1=sQuery(id+"F5.wireOp",EDGE,"E16");var subQ2=makeQuery(id+"F5.imprint","INTERSECT",VERTEX,{"disambiguationData":[OD(0.0)],"derivedFrom":[subQ1,subQ0]});Q1=makeQuery(id+"F5.imprint","IMPRINT",FACE,{"disambiguationData":[TD([[makeQuery(id+"F5.imprint","IMPRINT",EDGE,{"disambiguationData":[TD([[subQ2,-1.0]])],"derivedFrom":subQ1}),1.0]])]});}
            var Q2;
            {var subQ0=sQuery(id+"F5.wireOp",EDGE,"E35");var subQ1=sQuery(id+"F5.wireOp",EDGE,"E16");var subQ2=makeQuery(id+"F5.imprint","INTERSECT",VERTEX,{"disambiguationData":[OD(0.0)],"derivedFrom":[subQ1,subQ0]});Q2=makeQuery(id+"F5.imprint","IMPRINT",FACE,{"disambiguationData":[TD([[makeQuery(id+"F5.imprint","IMPRINT",EDGE,{"disambiguationData":[TD([[subQ2,-1.0]])],"derivedFrom":subQ1}),-1.0]])]});}
            var Q3;
            {var subQ0=sQuery(id+"F5.wireOp",EDGE,"E35");var subQ1=sQuery(id+"F5.wireOp",EDGE,"E16");var subQ2=makeQuery(id+"F5.imprint","INTERSECT",VERTEX,{"disambiguationData":[OD(0.0)],"derivedFrom":[subQ1,subQ0]});Q3=makeQuery(id+"F5.imprint","IMPRINT",FACE,{"disambiguationData":[TD([[makeQuery(id+"F5.imprint","IMPRINT",EDGE,{"disambiguationData":[TD([[subQ2,-1.0]])],"derivedFrom":subQ1}),1.0]])]});}
            var Q4;
            {var subQ0=sQuery(id+"F5.wireOp",EDGE,"E36");var subQ1=sQuery(id+"F5.wireOp",EDGE,"E16");var subQ2=makeQuery(id+"F5.imprint","INTERSECT",VERTEX,{"disambiguationData":[OD(0.0)],"derivedFrom":[subQ1,subQ0]});Q4=makeQuery(id+"F5.imprint","IMPRINT",FACE,{"disambiguationData":[TD([[makeQuery(id+"F5.imprint","IMPRINT",EDGE,{"disambiguationData":[TD([[subQ2,-1.0]])],"derivedFrom":subQ1}),1.0]])]});}
            var Q5;
            {var subQ0=sQuery(id+"F5.wireOp",EDGE,"E36");var subQ1=sQuery(id+"F5.wireOp",EDGE,"E16");var subQ2=makeQuery(id+"F5.imprint","INTERSECT",VERTEX,{"disambiguationData":[OD(0.0)],"derivedFrom":[subQ1,subQ0]});Q5=makeQuery(id+"F5.imprint","IMPRINT",FACE,{"disambiguationData":[TD([[makeQuery(id+"F5.imprint","IMPRINT",EDGE,{"disambiguationData":[TD([[subQ2,-1.0]])],"derivedFrom":subQ1}),-1.0]])]});}
            var Q6;
            {var subQ0=sQuery(id+"F5.wireOp",EDGE,"E37");var subQ1=sQuery(id+"F5.wireOp",EDGE,"E16");var subQ2=makeQuery(id+"F5.imprint","INTERSECT",VERTEX,{"disambiguationData":[OD(0.0)],"derivedFrom":[subQ1,subQ0]});Q6=makeQuery(id+"F5.imprint","IMPRINT",FACE,{"disambiguationData":[TD([[makeQuery(id+"F5.imprint","IMPRINT",EDGE,{"disambiguationData":[TD([[subQ2,-1.0]])],"derivedFrom":subQ1}),1.0]])]});}
            var Q7;
            {var subQ0=sQuery(id+"F5.wireOp",EDGE,"E37");var subQ1=sQuery(id+"F5.wireOp",EDGE,"E16");var subQ2=makeQuery(id+"F5.imprint","INTERSECT",VERTEX,{"disambiguationData":[OD(0.0)],"derivedFrom":[subQ1,subQ0]});Q7=makeQuery(id+"F5.imprint","IMPRINT",FACE,{"disambiguationData":[TD([[makeQuery(id+"F5.imprint","IMPRINT",EDGE,{"disambiguationData":[TD([[subQ2,-1.0]])],"derivedFrom":subQ1}),-1.0]])]});}
            var Q8;
            {var subQ1=sQuery(id+"F5.wireOp",EDGE,"E39.bottom");Q8=makeQuery(id+"F5.imprint","IMPRINT",FACE,{"disambiguationData":[TD([[makeQuery(id+"F5.imprint","IMPRINT",EDGE,{"derivedFrom":subQ1}),-1.0]])]});}
            var Q9;
            {var subQ0=sQuery(id+"F5.wireOp",EDGE,"E39.top");var subQ1=sQuery(id+"F5.wireOp",EDGE,"E16");var subQ2=makeQuery(id+"F5.imprint","INTERSECT",VERTEX,{"derivedFrom":[subQ1,subQ0]});Q9=makeQuery(id+"F5.imprint","IMPRINT",FACE,{"disambiguationData":[TD([[makeQuery(id+"F5.imprint","IMPRINT",EDGE,{"disambiguationData":[TD([[subQ2,-1.0]])],"derivedFrom":subQ1}),1.0]])]});}
            var Q10;
            {var subQ0=sQuery(id+"F5.wireOp",EDGE,"E38");var subQ1=sQuery(id+"F5.wireOp",EDGE,"E16");var subQ2=makeQuery(id+"F5.imprint","INTERSECT",VERTEX,{"disambiguationData":[OD(0.0)],"derivedFrom":[subQ1,subQ0]});Q10=makeQuery(id+"F5.imprint","IMPRINT",FACE,{"disambiguationData":[TD([[makeQuery(id+"F5.imprint","IMPRINT",EDGE,{"disambiguationData":[TD([[subQ2,-1.0]])],"derivedFrom":subQ1}),-1.0]])]});}
            var Q11;
            {var subQ0=sQuery(id+"F5.wireOp",EDGE,"E38");var subQ1=sQuery(id+"F5.wireOp",EDGE,"E16");var subQ2=makeQuery(id+"F5.imprint","INTERSECT",VERTEX,{"disambiguationData":[OD(0.0)],"derivedFrom":[subQ1,subQ0]});Q11=makeQuery(id+"F5.imprint","IMPRINT",FACE,{"disambiguationData":[TD([[makeQuery(id+"F5.imprint","IMPRINT",EDGE,{"disambiguationData":[TD([[subQ2,-1.0]])],"derivedFrom":subQ1}),1.0]])]});}
            extrude(context, id + "F8", {"entities" : qUnion([Q0, Q1, Q2, Q3, Q4, Q5, Q6, Q7, Q8, Q9, Q10, Q11]), "operationType" : NewBodyOperationType.ADD, "depth" : 8 * mm, "offsetDistance" : 25 * mm});
        }
        {
            var Q0;
            Q0=makeQuery(id+"F8.opExtrude","CAP_EDGE",EDGE,{"disambiguationData":[OSD([sQuery(id+"F5.wireOp",EDGE,"E38")])],"isStart":false});
            var Q1;
            Q1=makeQuery(id+"F8.opExtrude","CAP_FACE",FACE,{"disambiguationData":[OSD([sQuery(id+"F5.wireOp",EDGE,"E34")])],"isStart":false});
            var Q2;
            Q2=makeQuery(id+"F8.opExtrude","CAP_FACE",FACE,{"disambiguationData":[OSD([sQuery(id+"F5.wireOp",EDGE,"E35")])],"isStart":false});
            var Q3;
            Q3=makeQuery(id+"F8.opExtrude","CAP_FACE",FACE,{"disambiguationData":[OSD([sQuery(id+"F5.wireOp",EDGE,"E36")])],"isStart":false});
            var Q4;
            Q4=makeQuery(id+"F8.opExtrude","CAP_FACE",FACE,{"disambiguationData":[OSD([sQuery(id+"F5.wireOp",EDGE,"E37")])],"isStart":false});
            var Q5;
            Q5=makeQuery(id+"F8.opExtrude","CAP_EDGE",EDGE,{"disambiguationData":[OSD([sQuery(id+"F5.wireOp",EDGE,"E39.left")])],"isStart":false});
            var Q6;
            Q6=makeQuery(id+"F8.opExtrude","CAP_EDGE",EDGE,{"disambiguationData":[OSD([sQuery(id+"F5.wireOp",EDGE,"E39.right")])],"isStart":false});
            var Q7;
            Q7=makeQuery(id+"F8.opExtrude","CAP_EDGE",EDGE,{"disambiguationData":[OSD([sQuery(id+"F5.wireOp",EDGE,"E39.bottom")])],"isStart":false});
            var Q8;
            Q8=makeQuery(id+"F8.opExtrude","CAP_EDGE",EDGE,{"disambiguationData":[OSD([sQuery(id+"F5.wireOp",EDGE,"E39.top")])],"isStart":false});
            fillet(context, id + "F9", {"entities" : qUnion([Q0, Q1, Q2, Q3, Q4, Q5, Q6, Q7, Q8]), "radius" : .45 * mm, "tangentPropagation" : true, "allowEdgeOverflow" : false});
        }
        {
            var Q0;
            Q0=qCreatedBy(makeId("Top.planeOp"),FACE);
            var sketch = newSketch(context, id + "F10", { "sketchPlane" : qUnion([Q0])});
            skCircle(sketch, "E40", {"center": v(0, 0) * mm, "radius": 13.47 * mm});
            skSolve(sketch);
        }
        {
            var Q0;
            Q0=makeQuery(id+"F10.imprint","IMPRINT",FACE,{"disambiguationData":[TD([[makeQuery(id+"F10.imprint","IMPRINT",EDGE,{"derivedFrom":sQuery(id+"F10.wireOp",EDGE,"E40")}),1.0]])]});
            extrude(context, id + "F11", {"entities" : qUnion([Q0]), "operationType" : NewBodyOperationType.REMOVE, "depth" : 1 * mm, "offsetDistance" : 25 * mm});
        }
        {
            var Q0;
            {var subQ0=sQuery(id+"F0.wireOp",EDGE,"E7.bottom");var subQ1=sQuery(id+"F0.wireOp",EDGE,"E1.0");var subQ2=makeQuery(id+"F0.imprint","INTERSECT",VERTEX,{"disambiguationData":[OD(1.0)],"derivedFrom":[subQ1,subQ0]});Q0=makeQuery(id+"F0.imprint","IMPRINT",FACE,{"disambiguationData":[TD([[makeQuery(id+"F0.imprint","IMPRINT",EDGE,{"disambiguationData":[TD([[subQ2,-1.0]])],"derivedFrom":subQ1}),1.0]])]});}
            var Q1;
            {var subQ0=sQuery(id+"F0.wireOp",EDGE,"E3.left");var subQ1=sQuery(id+"F0.wireOp",EDGE,"E1.0");var subQ2=makeQuery(id+"F0.imprint","INTERSECT",VERTEX,{"disambiguationData":[OD(0.0)],"derivedFrom":[subQ1,subQ0]});Q1=makeQuery(id+"F0.imprint","IMPRINT",FACE,{"disambiguationData":[TD([[makeQuery(id+"F0.imprint","IMPRINT",EDGE,{"disambiguationData":[TD([[subQ2,-1.0]])],"derivedFrom":subQ1}),1.0]])]});}
            var Q2;
            {var subQ0=sQuery(id+"F0.wireOp",EDGE,"E8.left");var subQ1=sQuery(id+"F0.wireOp",EDGE,"E1.0");var subQ2=makeQuery(id+"F0.imprint","INTERSECT",VERTEX,{"disambiguationData":[OD(0.0)],"derivedFrom":[subQ1,subQ0]});Q2=makeQuery(id+"F0.imprint","IMPRINT",FACE,{"disambiguationData":[TD([[makeQuery(id+"F0.imprint","IMPRINT",EDGE,{"disambiguationData":[TD([[subQ2,-1.0]])],"derivedFrom":subQ1}),1.0]])]});}
            var Q3;
            {var subQ0=sQuery(id+"F0.wireOp",EDGE,"E9.left");var subQ1=sQuery(id+"F0.wireOp",EDGE,"E1.0");var subQ2=makeQuery(id+"F0.imprint","INTERSECT",VERTEX,{"disambiguationData":[OD(0.0)],"derivedFrom":[subQ1,subQ0]});Q3=makeQuery(id+"F0.imprint","IMPRINT",FACE,{"disambiguationData":[TD([[makeQuery(id+"F0.imprint","IMPRINT",EDGE,{"disambiguationData":[TD([[subQ2,-1.0]])],"derivedFrom":subQ1}),1.0]])]});}
            var Q4;
            {var subQ0=sQuery(id+"F0.wireOp",EDGE,"E7.top");var subQ1=sQuery(id+"F0.wireOp",EDGE,"E1.0");var subQ2=makeQuery(id+"F0.imprint","INTERSECT",VERTEX,{"disambiguationData":[OD(0.0)],"derivedFrom":[subQ1,subQ0]});Q4=makeQuery(id+"F0.imprint","IMPRINT",FACE,{"disambiguationData":[TD([[makeQuery(id+"F0.imprint","IMPRINT",EDGE,{"disambiguationData":[TD([[subQ2,-1.0]])],"derivedFrom":subQ1}),1.0]])]});}
            var Q5;
            {var subQ0=sQuery(id+"F0.wireOp",EDGE,"E6.top");var subQ1=sQuery(id+"F0.wireOp",EDGE,"E1.0");var subQ2=makeQuery(id+"F0.imprint","INTERSECT",VERTEX,{"disambiguationData":[OD(0.0)],"derivedFrom":[subQ1,subQ0]});Q5=makeQuery(id+"F0.imprint","IMPRINT",FACE,{"disambiguationData":[TD([[makeQuery(id+"F0.imprint","IMPRINT",EDGE,{"disambiguationData":[TD([[subQ2,-1.0]])],"derivedFrom":subQ1}),1.0]])]});}
            var Q6;
            {var subQ0=sQuery(id+"F0.wireOp",EDGE,"E3.right");var subQ1=sQuery(id+"F0.wireOp",EDGE,"E1.0");var subQ2=makeQuery(id+"F0.imprint","INTERSECT",VERTEX,{"disambiguationData":[OD(1.0)],"derivedFrom":[subQ1,subQ0]});Q6=makeQuery(id+"F0.imprint","IMPRINT",FACE,{"disambiguationData":[TD([[makeQuery(id+"F0.imprint","IMPRINT",EDGE,{"disambiguationData":[TD([[subQ2,-1.0]])],"derivedFrom":subQ1}),1.0]])]});}
            extrude(context, id + "F12", {"entities" : qUnion([Q0, Q1, Q2, Q3, Q4, Q5, Q6]), "operationType" : NewBodyOperationType.REMOVE, "depth" : 1 * mm, "offsetDistance" : 25 * mm});
        }
        {
            var Q0;
            {var subQ0=sQuery(id+"F0.wireOp",EDGE,"E7.bottom");var subQ1=sQuery(id+"F0.wireOp",EDGE,"E1.0");Q0=makeQuery(id+"F12.boolean.opBoolean","COPY",EDGE,{"derivedFrom":makeQuery(id+"F12.opExtrude","SWEPT_EDGE",EDGE,{"disambiguationData":[OSD([subQ1,subQ0]),TDD([makeQuery(id+"F0.imprint","INTERSECT",VERTEX,{"disambiguationData":[OD(1.0)],"derivedFrom":[subQ1,subQ0]})])]})});}
            var Q1;
            {var subQ0=sQuery(id+"F0.wireOp",EDGE,"E3.left");var subQ1=sQuery(id+"F0.wireOp",EDGE,"E1.0");Q1=makeQuery(id+"F12.boolean.opBoolean","COPY",EDGE,{"derivedFrom":makeQuery(id+"F12.opExtrude","SWEPT_EDGE",EDGE,{"disambiguationData":[OSD([subQ1,subQ0]),TDD([makeQuery(id+"F0.imprint","INTERSECT",VERTEX,{"disambiguationData":[OD(0.0)],"derivedFrom":[subQ1,subQ0]})])]})});}
            var Q2;
            Q2=makeQuery(id+"F12.boolean.opBoolean","COPY",EDGE,{"derivedFrom":makeQuery(id+"F12.opExtrude","SWEPT_EDGE",EDGE,{"disambiguationData":[OSD([sQuery(id+"F0.wireOp",EDGE,"E1.0"),sQuery(id+"F0.wireOp",EDGE,"E8.left")])]})});
            var Q3;
            Q3=makeQuery(id+"F12.boolean.opBoolean","COPY",EDGE,{"derivedFrom":makeQuery(id+"F12.opExtrude","SWEPT_EDGE",EDGE,{"disambiguationData":[OSD([sQuery(id+"F0.wireOp",EDGE,"E1.0"),sQuery(id+"F0.wireOp",EDGE,"E9.left")])]})});
            var Q4;
            Q4=makeQuery(id+"F12.boolean.opBoolean","COPY",EDGE,{"derivedFrom":makeQuery(id+"F12.opExtrude","SWEPT_EDGE",EDGE,{"disambiguationData":[OSD([sQuery(id+"F0.wireOp",EDGE,"E1.0"),sQuery(id+"F0.wireOp",EDGE,"E9.right")])]})});
            var Q5;
            Q5=makeQuery(id+"F12.boolean.opBoolean","COPY",EDGE,{"derivedFrom":makeQuery(id+"F12.opExtrude","SWEPT_EDGE",EDGE,{"disambiguationData":[OSD([sQuery(id+"F0.wireOp",EDGE,"E1.0"),sQuery(id+"F0.wireOp",EDGE,"E7.top")])]})});
            var Q6;
            {var subQ0=sQuery(id+"F0.wireOp",EDGE,"E7.bottom");var subQ1=sQuery(id+"F0.wireOp",EDGE,"E1.0");Q6=makeQuery(id+"F12.boolean.opBoolean","COPY",EDGE,{"derivedFrom":makeQuery(id+"F12.opExtrude","SWEPT_EDGE",EDGE,{"disambiguationData":[OSD([subQ1,subQ0]),TDD([makeQuery(id+"F0.imprint","INTERSECT",VERTEX,{"disambiguationData":[OD(0.0)],"derivedFrom":[subQ1,subQ0]})])]})});}
            var Q7;
            {var subQ0=sQuery(id+"F0.wireOp",EDGE,"E6.top");var subQ1=sQuery(id+"F0.wireOp",EDGE,"E1.0");Q7=makeQuery(id+"F12.boolean.opBoolean","COPY",EDGE,{"derivedFrom":makeQuery(id+"F12.opExtrude","SWEPT_EDGE",EDGE,{"disambiguationData":[OSD([subQ1,subQ0]),TDD([makeQuery(id+"F0.imprint","INTERSECT",VERTEX,{"disambiguationData":[OD(0.0)],"derivedFrom":[subQ1,subQ0]})])]})});}
            var Q8;
            Q8=makeQuery(id+"F12.boolean.opBoolean","COPY",EDGE,{"derivedFrom":makeQuery(id+"F12.opExtrude","SWEPT_EDGE",EDGE,{"disambiguationData":[OSD([sQuery(id+"F0.wireOp",EDGE,"E1.0"),sQuery(id+"F0.wireOp",EDGE,"E6.bottom")])]})});
            var Q9;
            Q9=makeQuery(id+"F12.boolean.opBoolean","COPY",EDGE,{"derivedFrom":makeQuery(id+"F12.opExtrude","SWEPT_EDGE",EDGE,{"disambiguationData":[OSD([sQuery(id+"F0.wireOp",EDGE,"E1.0"),sQuery(id+"F0.wireOp",EDGE,"E3.right")])]})});
            var Q10;
            {var subQ0=sQuery(id+"F0.wireOp",EDGE,"E3.left");var subQ1=sQuery(id+"F0.wireOp",EDGE,"E1.0");Q10=makeQuery(id+"F12.boolean.opBoolean","COPY",EDGE,{"derivedFrom":makeQuery(id+"F12.opExtrude","SWEPT_EDGE",EDGE,{"disambiguationData":[OSD([subQ1,subQ0]),TDD([makeQuery(id+"F0.imprint","INTERSECT",VERTEX,{"disambiguationData":[OD(1.0)],"derivedFrom":[subQ1,subQ0]})])]})});}
            var Q11;
            Q11=makeQuery(id+"F12.boolean.opBoolean","COPY",EDGE,{"derivedFrom":makeQuery(id+"F12.opExtrude","SWEPT_EDGE",EDGE,{"disambiguationData":[OSD([sQuery(id+"F0.wireOp",EDGE,"E1.0"),sQuery(id+"F0.wireOp",EDGE,"E2.left")])]})});
            var Q12;
            {var subQ0=sQuery(id+"F0.wireOp",EDGE,"E6.top");var subQ1=sQuery(id+"F0.wireOp",EDGE,"E1.0");Q12=makeQuery(id+"F12.boolean.opBoolean","COPY",EDGE,{"derivedFrom":makeQuery(id+"F12.opExtrude","SWEPT_EDGE",EDGE,{"disambiguationData":[OSD([subQ1,subQ0]),TDD([makeQuery(id+"F0.imprint","INTERSECT",VERTEX,{"disambiguationData":[OD(1.0)],"derivedFrom":[subQ1,subQ0]})])]})});}
            var Q13;
            Q13=makeQuery(id+"F12.boolean.opBoolean","COPY",EDGE,{"derivedFrom":makeQuery(id+"F12.opExtrude","SWEPT_EDGE",EDGE,{"disambiguationData":[OSD([sQuery(id+"F0.wireOp",EDGE,"E1.0"),sQuery(id+"F0.wireOp",EDGE,"E2.right")])]})});
            fillet(context, id + "F13", {"entities" : qUnion([Q0, Q1, Q2, Q3, Q4, Q5, Q6, Q7, Q8, Q9, Q10, Q11, Q12, Q13]), "radius" : 1 * mm, "tangentPropagation" : true, "allowEdgeOverflow" : false});
        }
        {
            var Q0;
            {var subQ0=sQuery(id+"F0.wireOp",EDGE,"E11");var subQ1=sQuery(id+"F0.wireOp",EDGE,"E8.right");var subQ2=makeQuery(id+"F0.imprint","INTERSECT",VERTEX,{"disambiguationData":[OD(1.0)],"derivedFrom":[subQ1,subQ0]});Q0=makeQuery(id+"F0.imprint","IMPRINT",FACE,{"disambiguationData":[TD([[makeQuery(id+"F0.imprint","IMPRINT",EDGE,{"disambiguationData":[TD([[subQ2,-1.0]])],"derivedFrom":subQ1}),1.0]])]});}
            var Q1;
            {var subQ0=sQuery(id+"F0.wireOp",EDGE,"E11");var subQ1=sQuery(id+"F0.wireOp",EDGE,"E9.left");var subQ2=makeQuery(id+"F0.imprint","INTERSECT",VERTEX,{"disambiguationData":[OD(1.0)],"derivedFrom":[subQ1,subQ0]});Q1=makeQuery(id+"F0.imprint","IMPRINT",FACE,{"disambiguationData":[TD([[makeQuery(id+"F0.imprint","IMPRINT",EDGE,{"disambiguationData":[TD([[subQ2,-1.0]])],"derivedFrom":subQ1}),1.0]])]});}
            var Q2;
            {var subQ0=sQuery(id+"F0.wireOp",EDGE,"E11");var subQ1=sQuery(id+"F0.wireOp",EDGE,"E8.left");var subQ2=makeQuery(id+"F0.imprint","INTERSECT",VERTEX,{"disambiguationData":[OD(1.0)],"derivedFrom":[subQ1,subQ0]});Q2=makeQuery(id+"F0.imprint","IMPRINT",FACE,{"disambiguationData":[TD([[makeQuery(id+"F0.imprint","IMPRINT",EDGE,{"disambiguationData":[TD([[subQ2,-1.0]])],"derivedFrom":subQ1}),1.0]])]});}
            var Q3;
            {var subQ0=sQuery(id+"F0.wireOp",EDGE,"E11");var subQ5=sQuery(id+"F0.wireOp",EDGE,"E9.right");var subQ6=makeQuery(id+"F0.imprint","INTERSECT",VERTEX,{"disambiguationData":[OD(1.0)],"derivedFrom":[subQ5,subQ0]});Q3=makeQuery(id+"F0.imprint","IMPRINT",FACE,{"disambiguationData":[TD([[makeQuery(id+"F0.imprint","IMPRINT",EDGE,{"disambiguationData":[TD([[subQ6,-1.0]])],"derivedFrom":subQ5}),1.0]])]});}
            var Q4;
            {var subQ0=sQuery(id+"F0.wireOp",EDGE,"E11");var subQ5=sQuery(id+"F0.wireOp",EDGE,"E8.left");var subQ6=makeQuery(id+"F0.imprint","INTERSECT",VERTEX,{"disambiguationData":[OD(1.0)],"derivedFrom":[subQ5,subQ0]});Q4=makeQuery(id+"F0.imprint","IMPRINT",FACE,{"disambiguationData":[TD([[makeQuery(id+"F0.imprint","IMPRINT",EDGE,{"disambiguationData":[TD([[subQ6,-1.0]])],"derivedFrom":subQ5}),-1.0]])]});}
            var Q5;
            {var subQ0=sQuery(id+"F0.wireOp",EDGE,"E12");Q5=makeQuery(id+"F0.imprint","IMPRINT",FACE,{"disambiguationData":[TD([[makeQuery(id+"F0.imprint","IMPRINT",EDGE,{"derivedFrom":subQ0}),-1.0]])]});}
            var Q6;
            {var subQ0=sQuery(id+"F0.wireOp",EDGE,"E13");Q6=makeQuery(id+"F0.imprint","IMPRINT",FACE,{"disambiguationData":[TD([[makeQuery(id+"F0.imprint","IMPRINT",EDGE,{"derivedFrom":subQ0}),-1.0]])]});}
            extrude(context, id + "F14", {"entities" : qUnion([Q0, Q1, Q2, Q3, Q4, Q5, Q6]), "operationType" : NewBodyOperationType.ADD, "depth" : 1 * mm, "offsetDistance" : 25 * mm});
        }
        {
            var Q0;
            Q0=qCreatedBy(makeId("Top.planeOp"),FACE);
            var sketch = newSketch(context, id + "F15", { "sketchPlane" : qUnion([Q0])});
            skCircle(sketch, "E41", {"center": v(0, 0) * mm, "radius": 19.4 * mm});
            skSolve(sketch);
        }
        {
            var Q0;
            Q0=makeQuery(id+"F15.imprint","IMPRINT",FACE,{"disambiguationData":[TD([[makeQuery(id+"F15.imprint","IMPRINT",EDGE,{"derivedFrom":sQuery(id+"F15.wireOp",EDGE,"E41")}),1.0]])]});
            extrude(context, id + "F16", {"entities" : qUnion([Q0]), "operationType" : NewBodyOperationType.ADD, "depth" : .2 * mm, "offsetDistance" : 25 * mm});
        }
        {
            var Q0;
            {var subQ0=sQuery(id+"F5.wireOp",EDGE,"E38");var subQ1=sQuery(id+"F5.wireOp",EDGE,"E16");var subQ2=makeQuery(id+"F5.imprint","INTERSECT",VERTEX,{"disambiguationData":[OD(0.0)],"derivedFrom":[subQ1,subQ0]});Q0=makeQuery(id+"F5.imprint","IMPRINT",FACE,{"disambiguationData":[TD([[makeQuery(id+"F5.imprint","IMPRINT",EDGE,{"disambiguationData":[TD([[subQ2,-1.0]])],"derivedFrom":subQ1}),-1.0]])]});}
            var Q1;
            {var subQ0=sQuery(id+"F5.wireOp",EDGE,"E38");var subQ1=sQuery(id+"F5.wireOp",EDGE,"E16");var subQ2=makeQuery(id+"F5.imprint","INTERSECT",VERTEX,{"disambiguationData":[OD(0.0)],"derivedFrom":[subQ1,subQ0]});Q1=makeQuery(id+"F5.imprint","IMPRINT",FACE,{"disambiguationData":[TD([[makeQuery(id+"F5.imprint","IMPRINT",EDGE,{"disambiguationData":[TD([[subQ2,-1.0]])],"derivedFrom":subQ1}),1.0]])]});}
            var Q2;
            {var subQ1=sQuery(id+"F5.wireOp",EDGE,"E39.bottom");Q2=makeQuery(id+"F5.imprint","IMPRINT",FACE,{"disambiguationData":[TD([[makeQuery(id+"F5.imprint","IMPRINT",EDGE,{"derivedFrom":subQ1}),-1.0]])]});}
            var Q3;
            {var subQ0=sQuery(id+"F5.wireOp",EDGE,"E39.top");var subQ1=sQuery(id+"F5.wireOp",EDGE,"E16");var subQ2=makeQuery(id+"F5.imprint","INTERSECT",VERTEX,{"derivedFrom":[subQ1,subQ0]});Q3=makeQuery(id+"F5.imprint","IMPRINT",FACE,{"disambiguationData":[TD([[makeQuery(id+"F5.imprint","IMPRINT",EDGE,{"disambiguationData":[TD([[subQ2,-1.0]])],"derivedFrom":subQ1}),1.0]])]});}
            var Q4;
            {var subQ0=sQuery(id+"F5.wireOp",EDGE,"E37");var subQ1=sQuery(id+"F5.wireOp",EDGE,"E16");var subQ2=makeQuery(id+"F5.imprint","INTERSECT",VERTEX,{"disambiguationData":[OD(0.0)],"derivedFrom":[subQ1,subQ0]});Q4=makeQuery(id+"F5.imprint","IMPRINT",FACE,{"disambiguationData":[TD([[makeQuery(id+"F5.imprint","IMPRINT",EDGE,{"disambiguationData":[TD([[subQ2,-1.0]])],"derivedFrom":subQ1}),1.0]])]});}
            var Q5;
            {var subQ0=sQuery(id+"F5.wireOp",EDGE,"E37");var subQ1=sQuery(id+"F5.wireOp",EDGE,"E16");var subQ2=makeQuery(id+"F5.imprint","INTERSECT",VERTEX,{"disambiguationData":[OD(0.0)],"derivedFrom":[subQ1,subQ0]});Q5=makeQuery(id+"F5.imprint","IMPRINT",FACE,{"disambiguationData":[TD([[makeQuery(id+"F5.imprint","IMPRINT",EDGE,{"disambiguationData":[TD([[subQ2,-1.0]])],"derivedFrom":subQ1}),-1.0]])]});}
            var Q6;
            {var subQ0=sQuery(id+"F5.wireOp",EDGE,"E36");var subQ1=sQuery(id+"F5.wireOp",EDGE,"E16");var subQ2=makeQuery(id+"F5.imprint","INTERSECT",VERTEX,{"disambiguationData":[OD(0.0)],"derivedFrom":[subQ1,subQ0]});Q6=makeQuery(id+"F5.imprint","IMPRINT",FACE,{"disambiguationData":[TD([[makeQuery(id+"F5.imprint","IMPRINT",EDGE,{"disambiguationData":[TD([[subQ2,-1.0]])],"derivedFrom":subQ1}),1.0]])]});}
            var Q7;
            {var subQ0=sQuery(id+"F5.wireOp",EDGE,"E36");var subQ1=sQuery(id+"F5.wireOp",EDGE,"E16");var subQ2=makeQuery(id+"F5.imprint","INTERSECT",VERTEX,{"disambiguationData":[OD(0.0)],"derivedFrom":[subQ1,subQ0]});Q7=makeQuery(id+"F5.imprint","IMPRINT",FACE,{"disambiguationData":[TD([[makeQuery(id+"F5.imprint","IMPRINT",EDGE,{"disambiguationData":[TD([[subQ2,-1.0]])],"derivedFrom":subQ1}),-1.0]])]});}
            var Q8;
            {var subQ0=sQuery(id+"F5.wireOp",EDGE,"E35");var subQ1=sQuery(id+"F5.wireOp",EDGE,"E16");var subQ2=makeQuery(id+"F5.imprint","INTERSECT",VERTEX,{"disambiguationData":[OD(0.0)],"derivedFrom":[subQ1,subQ0]});Q8=makeQuery(id+"F5.imprint","IMPRINT",FACE,{"disambiguationData":[TD([[makeQuery(id+"F5.imprint","IMPRINT",EDGE,{"disambiguationData":[TD([[subQ2,-1.0]])],"derivedFrom":subQ1}),1.0]])]});}
            var Q9;
            {var subQ0=sQuery(id+"F5.wireOp",EDGE,"E35");var subQ1=sQuery(id+"F5.wireOp",EDGE,"E16");var subQ2=makeQuery(id+"F5.imprint","INTERSECT",VERTEX,{"disambiguationData":[OD(0.0)],"derivedFrom":[subQ1,subQ0]});Q9=makeQuery(id+"F5.imprint","IMPRINT",FACE,{"disambiguationData":[TD([[makeQuery(id+"F5.imprint","IMPRINT",EDGE,{"disambiguationData":[TD([[subQ2,-1.0]])],"derivedFrom":subQ1}),-1.0]])]});}
            var Q10;
            {var subQ0=sQuery(id+"F5.wireOp",EDGE,"E34");var subQ1=sQuery(id+"F5.wireOp",EDGE,"E16");var subQ2=makeQuery(id+"F5.imprint","INTERSECT",VERTEX,{"disambiguationData":[OD(0.0)],"derivedFrom":[subQ1,subQ0]});Q10=makeQuery(id+"F5.imprint","IMPRINT",FACE,{"disambiguationData":[TD([[makeQuery(id+"F5.imprint","IMPRINT",EDGE,{"disambiguationData":[TD([[subQ2,-1.0]])],"derivedFrom":subQ1}),-1.0]])]});}
            var Q11;
            {var subQ0=sQuery(id+"F5.wireOp",EDGE,"E34");var subQ1=sQuery(id+"F5.wireOp",EDGE,"E16");var subQ2=makeQuery(id+"F5.imprint","INTERSECT",VERTEX,{"disambiguationData":[OD(0.0)],"derivedFrom":[subQ1,subQ0]});Q11=makeQuery(id+"F5.imprint","IMPRINT",FACE,{"disambiguationData":[TD([[makeQuery(id+"F5.imprint","IMPRINT",EDGE,{"disambiguationData":[TD([[subQ2,-1.0]])],"derivedFrom":subQ1}),1.0]])]});}
            extrude(context, id + "F17", {"entities" : qUnion([Q0, Q1, Q2, Q3, Q4, Q5, Q6, Q7, Q8, Q9, Q10, Q11]), "operationType" : NewBodyOperationType.REMOVE, "depth" : 1.8 * mm, "offsetDistance" : 25 * mm});
        }
    });
